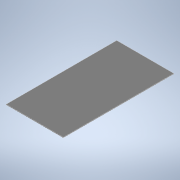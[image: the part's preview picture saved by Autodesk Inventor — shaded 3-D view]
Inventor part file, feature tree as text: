
AUTODESK INVENTOR PART (.ipt)
format: ipt  version: 2022 (Build 260153000, 153)  size: 102,912 bytes
history: native  units: mm
features: chamfer x3, extrude x1, sketch x1
ambient origin geometry x8: Origin, YZ Plane, XZ Plane, XY Plane, X Axis, Y Axis, Z Axis, Center Point
bodies: Solid1 (feature_tree)
feature tree (5):
  extrude  "Extrusion1"  Depth=56.8mm
  chamfer  "Chamfer1"  Distance=2.0mm
  chamfer  "Chamfer2"  Distance=2.0mm Angle=45.0deg
  chamfer  "Chamfer3"  Distance=2.0mm Angle=45.0deg
  sketch  "Sketch1"  dims[d0=110.0mm d1=56.8mm d2=2.0mm d3=0.0mm d4=1.5mm d5=2.0mm d6=45.0deg d7=1.5mm d8=2.0mm d9=45.0deg d10=1.5mm d11=2.0mm d12=45.0deg]
